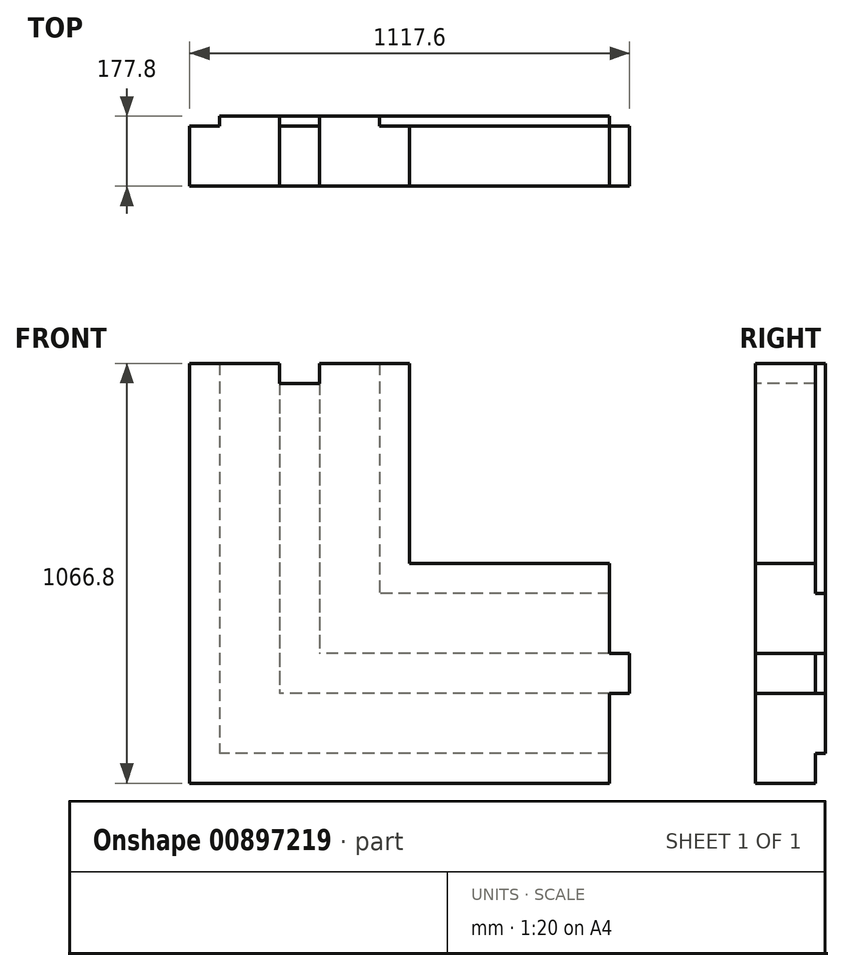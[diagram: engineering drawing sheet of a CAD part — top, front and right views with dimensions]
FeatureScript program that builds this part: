
annotation { "Feature Type Name" : "Feature", "Feature Type Description" : "" }
export const myFeature = defineFeature(function(context is Context, id is Id, definition is map)
    precondition{}
    {
        {
            var Q0;
            Q0=qCreatedBy(makeId("Top.planeOp"),FACE);
            var sketch = newSketch(context, id + "F0", { "sketchPlane" : qUnion([Q0])});
            skLineSegment(sketch, "E0", {"start": v(0, 0) * mm, "end": v(76.2, 0) * mm});
            skLineSegment(sketch, "E1", {"start": v(76.2, 0) * mm, "end": v(76.2, 25.4) * mm});
            skLineSegment(sketch, "E2", {"start": v(76.2, 25.4) * mm, "end": v(228.6, 25.4) * mm});
            skLineSegment(sketch, "E3", {"start": v(228.6, 25.4) * mm, "end": v(228.6, 0) * mm});
            skLineSegment(sketch, "E4", {"start": v(228.6, 0) * mm, "end": v(330.2, 0) * mm});
            skLineSegment(sketch, "E5", {"start": v(330.2, 0) * mm, "end": v(330.2, 25.4) * mm});
            skLineSegment(sketch, "E6", {"start": v(330.2, 25.4) * mm, "end": v(482.6, 25.4) * mm});
            skLineSegment(sketch, "E7", {"start": v(482.6, 25.4) * mm, "end": v(482.6, 0) * mm});
            skLineSegment(sketch, "E8", {"start": v(482.6, 0) * mm, "end": v(558.8, 0) * mm});
            skLineSegment(sketch, "E9", {"start": v(558.8, 0) * mm, "end": v(558.8, -152.4) * mm});
            skLineSegment(sketch, "E10", {"start": v(558.8, -152.4) * mm, "end": v(0, -152.4) * mm});
            skLineSegment(sketch, "E11", {"start": v(0, -152.4) * mm, "end": v(0, 0) * mm});
            skSolve(sketch);
        }
        {
            var Q0;
            Q0=qSketchRegion(id+"F0",true);
            extrude(context, id + "F1", {"entities" : qUnion([Q0]), "depth" : 1066.8 * mm, "offsetDistance" : 25.4 * mm});
        }
        {
            var Q0;
            Q0=makeQuery(id+"F1.opExtrude","SWEPT_FACE",FACE,{"disambiguationData":[OSD([sQuery(id+"F0.wireOp",EDGE,"E10")])]});
            cPlane(context, id + "F2", {"entities" : qUnion([Q0]), "cplaneType" : CPlaneType.OFFSET, "offset" : 0 * mm, "width" : 152.4 * mm, "height" : 152.4 * mm});
        }
        {
            var Q0;
            Q0=qCreatedBy(id+"F2.planeOp",FACE);
            var sketch = newSketch(context, id + "F3", { "sketchPlane" : qUnion([Q0])});
            skLineSegment(sketch, "E12.bottom", {"start": v(330.2, 1066.8) * mm, "end": v(228.6, 1066.8) * mm});
            skLineSegment(sketch, "E12.top", {"start": v(330.2, 1117.6) * mm, "end": v(228.6, 1117.6) * mm});
            skLineSegment(sketch, "E12.left", {"start": v(330.2, 1066.8) * mm, "end": v(330.2, 1117.6) * mm});
            skLineSegment(sketch, "E12.right", {"start": v(228.6, 1066.8) * mm, "end": v(228.6, 1117.6) * mm});
            skSolve(sketch);
        }
        {
            var Q0;
            Q0=qSketchRegion(id+"F3",true);
            extrude(context, id + "F4", {"entities" : qUnion([Q0]), "operationType" : NewBodyOperationType.ADD, "oppositeDirection" : true, "depth" : 152.4 * mm, "offsetDistance" : 25.4 * mm});
        }
        {
            var Q0;
            Q0=qCreatedBy(id+"F2.planeOp",FACE);
            var sketch = newSketch(context, id + "F5", { "sketchPlane" : qUnion([Q0])});
            skLineSegment(sketch, "E13.bottom", {"start": v(330.2, 0) * mm, "end": v(228.6, 0) * mm});
            skLineSegment(sketch, "E13.top", {"start": v(330.2, 50.8) * mm, "end": v(228.6, 50.8) * mm});
            skLineSegment(sketch, "E13.left", {"start": v(330.2, 0) * mm, "end": v(330.2, 50.8) * mm});
            skLineSegment(sketch, "E13.right", {"start": v(228.6, 0) * mm, "end": v(228.6, 50.8) * mm});
            skSolve(sketch);
        }
        {
            var Q0;
            Q0=qSketchRegion(id+"F5",true);
            extrude(context, id + "F6", {"entities" : qUnion([Q0]), "operationType" : NewBodyOperationType.REMOVE, "endBound" : BoundingType.THROUGH_ALL, "oppositeDirection" : true, "depth" : 25.4 * mm, "offsetDistance" : 25.4 * mm});
        }
        {
            var Q0;
            Q0=qCreatedBy(id+"F2.planeOp",FACE);
            var sketch = newSketch(context, id + "F7", { "sketchPlane" : qUnion([Q0])});
            skLineSegment(sketch, "E14", {"start": v(0, 0) * mm, "end": v(586.1, 586.1) * mm});
            skLineSegment(sketch, "E15", {"start": v(586.1, 586.1) * mm, "end": v(586.1, 0) * mm});
            skLineSegment(sketch, "E16", {"start": v(586.1, 0) * mm, "end": v(0, 0) * mm});
            skSolve(sketch);
        }
        {
            var Q0;
            Q0 = qSketchRegion(id + "F7", true);
            extrude(context, id + "F8", {"entities" : qUnion([Q0]), "operationType" : NewBodyOperationType.REMOVE, "endBound" : BoundingType.THROUGH_ALL, "oppositeDirection" : true, "depth" : 25.4 * mm, "offsetDistance" : 25.4 * mm});
        }
        {
            var Q0;
            Q0=makeQuery(id+"F1.opExtrude","SWEPT_BODY",BODY,{"disambiguationData":[OSD([sQuery(id+"F0.wireOp",EDGE,"E0"),sQuery(id+"F0.wireOp",EDGE,"E1"),sQuery(id+"F0.wireOp",EDGE,"E2"),sQuery(id+"F0.wireOp",EDGE,"E3"),sQuery(id+"F0.wireOp",EDGE,"E4"),sQuery(id+"F0.wireOp",EDGE,"E5"),sQuery(id+"F0.wireOp",EDGE,"E6"),sQuery(id+"F0.wireOp",EDGE,"E7"),sQuery(id+"F0.wireOp",EDGE,"E8"),sQuery(id+"F0.wireOp",EDGE,"E9"),sQuery(id+"F0.wireOp",EDGE,"E10"),sQuery(id+"F0.wireOp",EDGE,"E11")])]});
            var Q1;
            Q1=makeQuery(id+"F8.boolean.opBoolean","COPY",FACE,{"derivedFrom":makeQuery(id+"F8.opExtrude","SWEPT_FACE",FACE,{"disambiguationData":[OSD([sQuery(id+"F7.wireOp",EDGE,"E14")])]})});
            mirror(context, id + "F9", {"operationType" : NewBodyOperationType.ADD, "entities" : qUnion([Q0]), "mirrorPlane" : qUnion([Q1])});
        }
        {
            var Q0;
            Q0=qCreatedBy(id+"F2.planeOp",FACE);
            var sketch = newSketch(context, id + "F10", { "sketchPlane" : qUnion([Q0])});
            skLineSegment(sketch, "E17.bottom", {"start": v(330.2, 1117.6) * mm, "end": v(228.6, 1117.6) * mm});
            skLineSegment(sketch, "E17.top", {"start": v(330.2, 1016) * mm, "end": v(228.6, 1016) * mm});
            skLineSegment(sketch, "E17.left", {"start": v(330.2, 1117.6) * mm, "end": v(330.2, 1016) * mm});
            skLineSegment(sketch, "E17.right", {"start": v(228.6, 1117.6) * mm, "end": v(228.6, 1016) * mm});
            skSolve(sketch);
        }
        {
            var Q0;
            Q0 = qSketchRegion(id + "F10", true);
            extrude(context, id + "F11", {"entities" : qUnion([Q0]), "operationType" : NewBodyOperationType.REMOVE, "endBound" : BoundingType.THROUGH_ALL, "oppositeDirection" : true, "depth" : 25.4 * mm, "offsetDistance" : 25.4 * mm});
        }
    });
